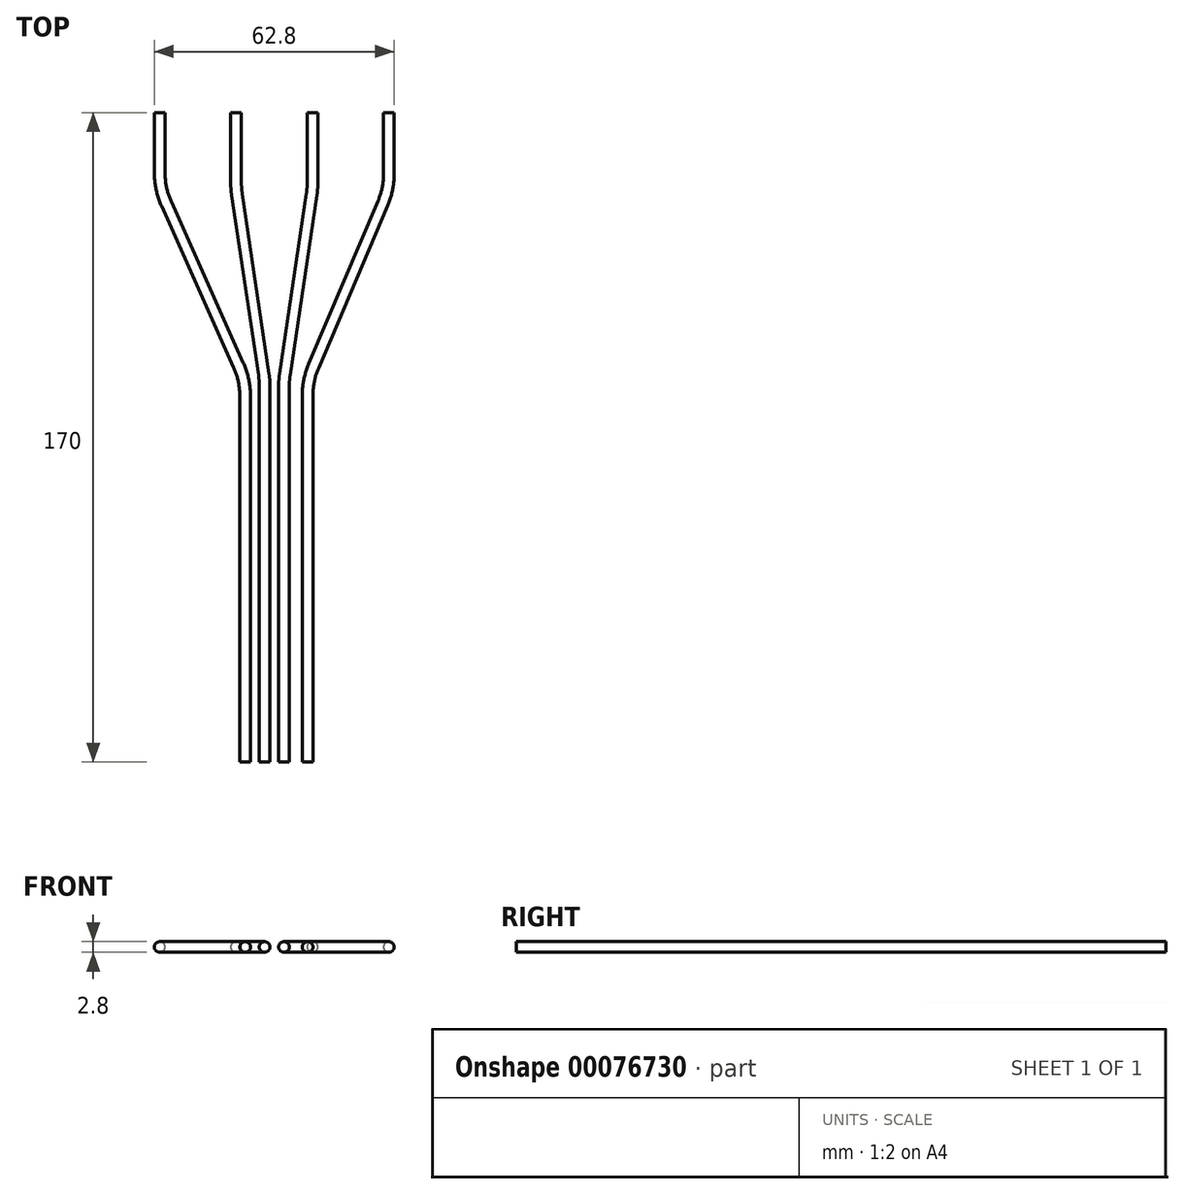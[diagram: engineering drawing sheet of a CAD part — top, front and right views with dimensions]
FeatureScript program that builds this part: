
annotation { "Feature Type Name" : "Feature", "Feature Type Description" : "" }
export const myFeature = defineFeature(function(context is Context, id is Id, definition is map)
    precondition{}
    {
        {
            var Q0;
            Q0=qCreatedBy(makeId("Top.planeOp"),FACE);
            var sketch = newSketch(context, id + "F0", { "sketchPlane" : qUnion([Q0])});
            skLineSegment(sketch, "E0", {"start": v(-7.62, 0) * mm, "end": v(-7.62, 95.73) * mm});
            skLineSegment(sketch, "E1", {"start": v(-9.37, 103.9) * mm, "end": v(-28.25, 146.1) * mm});
            skLineSegment(sketch, "E2", {"start": v(-30, 154.27) * mm, "end": v(-30, 170) * mm});
            skPoint(sketch, "E3.visualSharp", {"position": v(-7.62, 100) * mm});
            skArc(sketch, "E3.filletArc", {"start": v(-7.62, 95.73) * mm, "mid": v(-8.06, 99.9) * mm, "end": v(-9.37, 103.9) * mm});
            skPoint(sketch, "E4.visualSharp", {"position": v(-30, 150) * mm});
            skArc(sketch, "E4.filletArc", {"start": v(-30, 154.27) * mm, "mid": v(-29.56, 150.1) * mm, "end": v(-28.25, 146.1) * mm});
            skSolve(sketch);
        }
        {
            var Q0;
            Q0=qCreatedBy(makeId("Top.planeOp"),FACE);
            var sketch = newSketch(context, id + "F1", { "sketchPlane" : qUnion([Q0])});
            skLineSegment(sketch, "E5", {"start": v(-2.54, 0) * mm, "end": v(-2.54, 98.52) * mm});
            skLineSegment(sketch, "E6", {"start": v(-2.76, 101.47) * mm, "end": v(-9.78, 148.53) * mm});
            skLineSegment(sketch, "E7", {"start": v(-10, 151.48) * mm, "end": v(-10, 170) * mm});
            skPoint(sketch, "E8.visualSharp", {"position": v(-2.54, 100) * mm});
            skArc(sketch, "E8.filletArc", {"start": v(-2.54, 98.52) * mm, "mid": v(-2.6, 100) * mm, "end": v(-2.76, 101.47) * mm});
            skPoint(sketch, "E9.visualSharp", {"position": v(-10, 150) * mm});
            skArc(sketch, "E9.filletArc", {"start": v(-10, 151.48) * mm, "mid": v(-9.95, 150) * mm, "end": v(-9.78, 148.53) * mm});
            skSolve(sketch);
        }
        {
            var Q0;
            Q0=qCreatedBy(makeId("Top.planeOp"),FACE);
            var sketch = newSketch(context, id + "F2", { "sketchPlane" : qUnion([Q0])});
            skLineSegment(sketch, "E10", {"start": v(2.54, 0) * mm, "end": v(2.54, 98.52) * mm});
            skLineSegment(sketch, "E11", {"start": v(2.76, 101.47) * mm, "end": v(9.78, 148.53) * mm});
            skLineSegment(sketch, "E12", {"start": v(10, 151.48) * mm, "end": v(10, 170) * mm});
            skPoint(sketch, "E13.visualSharp", {"position": v(2.54, 100) * mm});
            skArc(sketch, "E13.filletArc", {"start": v(2.76, 101.47) * mm, "mid": v(2.6, 100) * mm, "end": v(2.54, 98.52) * mm});
            skPoint(sketch, "E14.visualSharp", {"position": v(10, 150) * mm});
            skArc(sketch, "E14.filletArc", {"start": v(9.78, 148.53) * mm, "mid": v(9.95, 150) * mm, "end": v(10, 151.48) * mm});
            skSolve(sketch);
        }
        {
            var Q0;
            Q0=qCreatedBy(makeId("Top.planeOp"),FACE);
            var sketch = newSketch(context, id + "F3", { "sketchPlane" : qUnion([Q0])});
            skLineSegment(sketch, "E15", {"start": v(8.72, 0) * mm, "end": v(8.72, 95.92) * mm});
            skLineSegment(sketch, "E16", {"start": v(10.32, 103.75) * mm, "end": v(28.4, 146.25) * mm});
            skLineSegment(sketch, "E17", {"start": v(30, 154.08) * mm, "end": v(30, 170) * mm});
            skPoint(sketch, "E18.visualSharp", {"position": v(8.72, 100) * mm});
            skArc(sketch, "E18.filletArc", {"start": v(10.32, 103.75) * mm, "mid": v(9.12, 99.92) * mm, "end": v(8.72, 95.92) * mm});
            skPoint(sketch, "E19.visualSharp", {"position": v(30, 150) * mm});
            skArc(sketch, "E19.filletArc", {"start": v(28.4, 146.25) * mm, "mid": v(29.6, 150.08) * mm, "end": v(30, 154.08) * mm});
            skSolve(sketch);
        }
        {
            var Q0;
            Q0=qCreatedBy(makeId("Front.planeOp"),FACE);
            var sketch = newSketch(context, id + "F4", { "sketchPlane" : qUnion([Q0])});
            skCircle(sketch, "E20", {"center": v(-7.62, 0) * mm, "radius": 1.4 * mm});
            skSolve(sketch);
        }
        {
            var Q0;
            Q0=qCreatedBy(makeId("Front.planeOp"),FACE);
            var sketch = newSketch(context, id + "F5", { "sketchPlane" : qUnion([Q0])});
            skCircle(sketch, "E21", {"center": v(-2.54, 0) * mm, "radius": 1.4 * mm});
            skSolve(sketch);
        }
        {
            var Q0;
            Q0=qCreatedBy(makeId("Front.planeOp"),FACE);
            var sketch = newSketch(context, id + "F6", { "sketchPlane" : qUnion([Q0])});
            skCircle(sketch, "E22", {"center": v(2.54, 0) * mm, "radius": 1.4 * mm});
            skSolve(sketch);
        }
        {
            var Q0;
            Q0=qCreatedBy(makeId("Front.planeOp"),FACE);
            var sketch = newSketch(context, id + "F7", { "sketchPlane" : qUnion([Q0])});
            skCircle(sketch, "E23", {"center": v(8.72, 0) * mm, "radius": 1.4 * mm});
            skSolve(sketch);
        }
        {
            var Q0;
            Q0=makeQuery(id+"F4.imprint","IMPRINT",FACE,{"disambiguationData":[TD([[makeQuery(id+"F4.imprint","IMPRINT",EDGE,{"derivedFrom":sQuery(id+"F4.wireOp",EDGE,"E20")}),1.0]])]});
            var Q1;
            Q1 = qConstructionFilter(qBodyType(qCreatedBy(id + "F0" ,EDGE), BodyType.WIRE), ConstructionObject.NO);
            sweep(context, id + "F8", {"profiles" : qUnion([Q0]), "path" : qUnion([Q1])});
        }
        {
            var Q0;
            Q0 = qSketchRegion(id + "F5", true);
            var Q1;
            Q1 = qConstructionFilter(qBodyType(qCreatedBy(id + "F1" ,EDGE), BodyType.WIRE), ConstructionObject.NO);
            sweep(context, id + "F9", {"profiles" : qUnion([Q0]), "path" : qUnion([Q1])});
        }
        {
            var Q0;
            Q0 = qSketchRegion(id + "F6", true);
            var Q1;
            Q1 = qConstructionFilter(qBodyType(qCreatedBy(id + "F2" ,EDGE), BodyType.WIRE), ConstructionObject.NO);
            sweep(context, id + "F10", {"profiles" : qUnion([Q0]), "path" : qUnion([Q1])});
        }
        {
            var Q0;
            Q0 = qSketchRegion(id + "F7", true);
            var Q1;
            Q1 = qConstructionFilter(qBodyType(qCreatedBy(id + "F3" ,EDGE), BodyType.WIRE), ConstructionObject.NO);
            sweep(context, id + "F11", {"profiles" : qUnion([Q0]), "path" : qUnion([Q1])});
        }
    });
